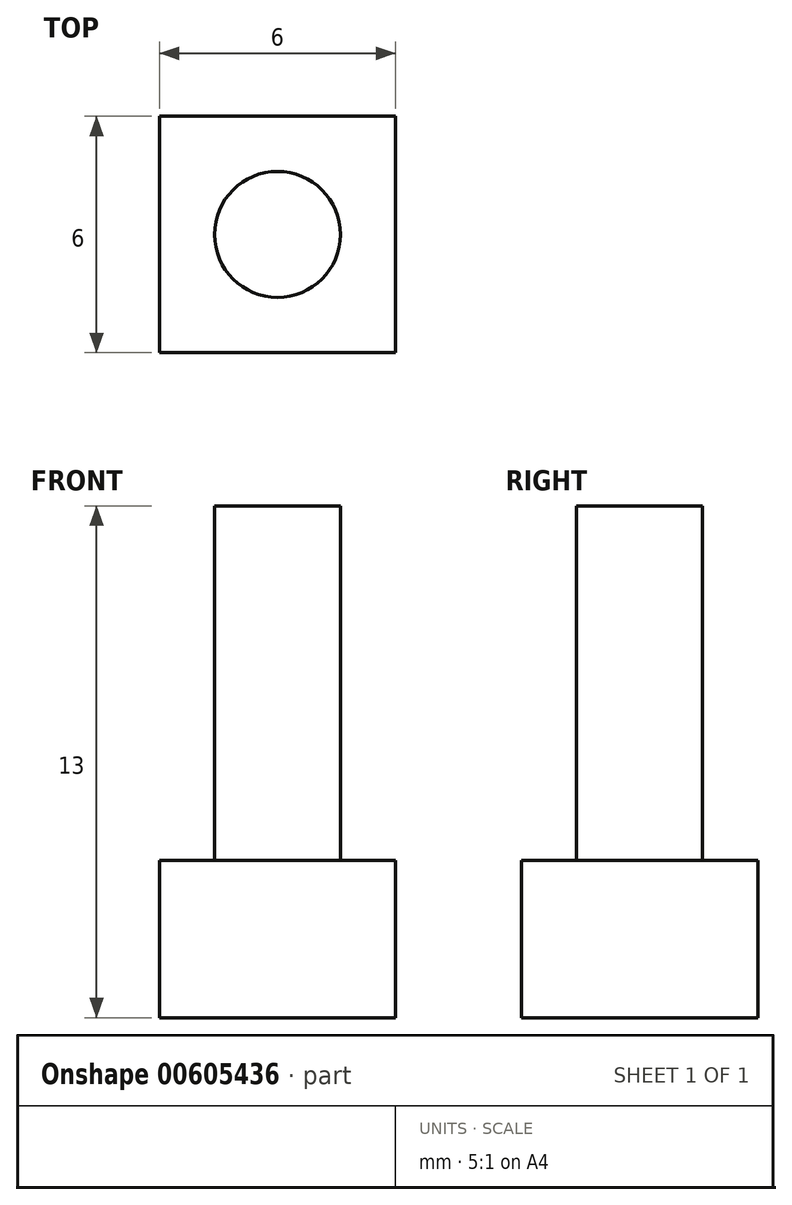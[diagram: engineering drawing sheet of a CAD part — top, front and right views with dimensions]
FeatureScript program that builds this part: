
annotation { "Feature Type Name" : "Feature", "Feature Type Description" : "" }
export const myFeature = defineFeature(function(context is Context, id is Id, definition is map)
    precondition{}
    {
        {
            var Q0;
            Q0=qCreatedBy(makeId("Top.planeOp"),FACE);
            var sketch = newSketch(context, id + "F0", { "sketchPlane" : qUnion([Q0])});
            skLineSegment(sketch, "E0.bottom", {"start": v(3, -3) * mm, "end": v(-3, -3) * mm});
            skLineSegment(sketch, "E0.top", {"start": v(3, 3) * mm, "end": v(-3, 3) * mm});
            skLineSegment(sketch, "E0.left", {"start": v(3, -3) * mm, "end": v(3, 3) * mm});
            skLineSegment(sketch, "E0.right", {"start": v(-3, -3) * mm, "end": v(-3, 3) * mm});
            skPoint(sketch, "E0.middle", {"position": v(0, 0) * mm});
            skCircle(sketch, "E1", {"center": v(0, 0) * mm, "radius": 1.6 * mm});
            skSolve(sketch);
        }
        {
            var Q0;
            Q0=makeQuery(id+"F0.imprint","IMPRINT",FACE,{"disambiguationData":[TD([[makeQuery(id+"F0.imprint","IMPRINT",EDGE,{"derivedFrom":sQuery(id+"F0.wireOp",EDGE,"E0.bottom")}),-1.0]])]});
            var Q1;
            Q1=makeQuery(id+"F0.imprint","IMPRINT",FACE,{"disambiguationData":[TD([[makeQuery(id+"F0.imprint","IMPRINT",EDGE,{"derivedFrom":sQuery(id+"F0.wireOp",EDGE,"E1")}),1.0]])]});
            extrude(context, id + "F1", {"entities" : qUnion([Q0, Q1]), "oppositeDirection" : true, "depth" : 4 * mm, "offsetDistance" : 25 * mm});
        }
        {
            var Q0;
            Q0=makeQuery(id+"F0.imprint","IMPRINT",FACE,{"disambiguationData":[TD([[makeQuery(id+"F0.imprint","IMPRINT",EDGE,{"derivedFrom":sQuery(id+"F0.wireOp",EDGE,"E1")}),1.0]])]});
            extrude(context, id + "F2", {"entities" : qUnion([Q0]), "operationType" : NewBodyOperationType.ADD, "depth" : 9 * mm, "offsetDistance" : 25 * mm});
        }
    });
